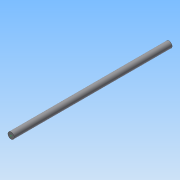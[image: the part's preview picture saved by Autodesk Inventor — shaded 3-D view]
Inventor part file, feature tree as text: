
AUTODESK INVENTOR PART (.ipt)
format: ipt  version: 2015 (Build 190159000, 159)  size: 71,680 bytes
history: native  units: mm
features: sketch x2, extrude x1
ambient origin geometry x8: Origin, YZ Plane, XZ Plane, XY Plane, X Axis, Y Axis, Z Axis, Center Point
bodies: Solid1 (feature_tree)
feature tree (3):
  extrude  "Extrusion1"  Depth=150.0mm TaperAngle=0.0deg
  sketch  "Sketch2"  dims[d3=100.0mm d4=0.0mm]
  sketch  "Sketch1"  dims[d0=10.0mm d1=150.0mm d2=0.0mm]
